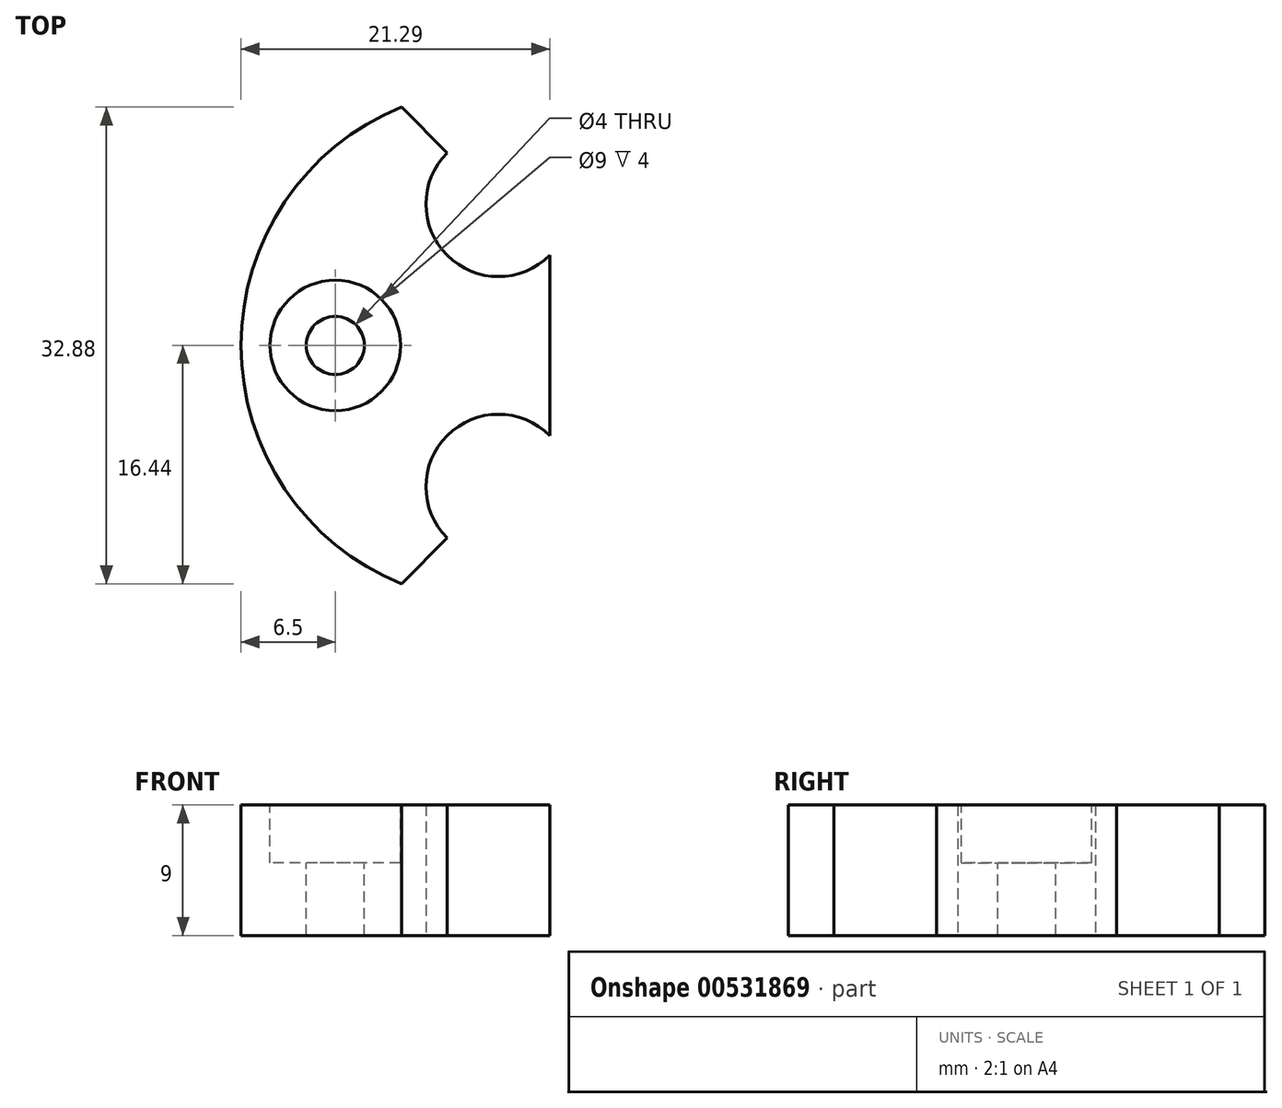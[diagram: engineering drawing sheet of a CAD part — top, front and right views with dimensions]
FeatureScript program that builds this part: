
annotation { "Feature Type Name" : "Feature", "Feature Type Description" : "" }
export const myFeature = defineFeature(function(context is Context, id is Id, definition is map)
    precondition{}
    {
        {
            var Q0;
            Q0=qCreatedBy(makeId("Top.planeOp"),FACE);
            var sketch = newSketch(context, id + "F0", { "sketchPlane" : qUnion([Q0])});
            skLineSegment(sketch, "E0", {"start": v(0, 0) * mm, "end": v(0, 50) * mm});
            skCircle(sketch, "E1", {"center": v(0, 50) * mm, "radius": 17.5 * mm});
            skLineSegment(sketch, "E2", {"start": v(0, 68.5) * mm, "end": v(0, 67.5) * mm});
            skLineSegment(sketch, "E3", {"start": v(0, 67.5) * mm, "end": v(0, 59.5) * mm});
            skLineSegment(sketch, "E4", {"start": v(0, 68.5) * mm, "end": v(0, 63.5) * mm});
            skLineSegment(sketch, "E5.1.0", {"start": v(-2.38, 63.61) * mm, "end": v(-2.38, 63.61) * mm});
            skLineSegment(sketch, "E5.2.0", {"start": v(-2.38, 55.39) * mm, "end": v(-2.38, 55.39) * mm});
            skPoint(sketch, "E5.center", {"position": v(0, 59.5) * mm});
            skLineSegment(sketch, "E6", {"start": v(-7, 59.72) * mm, "end": v(-7, 66.04) * mm});
            skLineSegment(sketch, "E7", {"start": v(7, 59.72) * mm, "end": v(7, 66.04) * mm});
            skCircle(sketch, "E8", {"center": v(0, 59.5) * mm, "radius": 4.75 * mm});
            skLineSegment(sketch, "E9", {"start": v(0, 59.5) * mm, "end": v(0, 54.5) * mm});
            skLineSegment(sketch, "E10", {"start": v(0, 54.5) * mm, "end": v(-3.14, 54.5) * mm});
            skLineSegment(sketch, "E11", {"start": v(0, 54.5) * mm, "end": v(3.14, 54.5) * mm});
            skLineSegment(sketch, "E12.trimOffspring", {"start": v(2.37, 55.39) * mm, "end": v(2.37, 55.39) * mm});
            skLineSegment(sketch, "E13", {"start": v(0, 50) * mm, "end": v(26.93, 50) * mm});
            skCircle(sketch, "E14.MirrorC", {"center": v(0, 40.5) * mm, "radius": 4.75 * mm});
            skEllipticalArc(sketch, "E15.MirrorCS", {});
            skLineSegment(sketch, "E16.MirrorCS", {"start": v(0, 45.5) * mm, "end": v(4.9, 45.5) * mm});
            skLineSegment(sketch, "E17.MirrorCS", {"start": v(0, 45.5) * mm, "end": v(-4.9, 45.5) * mm});
            skArc(sketch, "E18.MirrorCS", {"start": v(4.9, 45.5) * mm, "mid": v(6.45, 43.21) * mm, "end": v(7, 40.5) * mm});
            skArc(sketch, "E19.MirrorCS", {"start": v(-7, 40.5) * mm, "mid": v(-6.45, 43.21) * mm, "end": v(-4.9, 45.5) * mm});
            skLineSegment(sketch, "E20.MirrorCS", {"start": v(-7, 40.5) * mm, "end": v(-7, 33.96) * mm});
            skLineSegment(sketch, "E21.MirrorCS", {"start": v(7, 40.5) * mm, "end": v(7, 33.96) * mm});
            skLineSegment(sketch, "E22", {"start": v(0, 59.5) * mm, "end": v(-6.02, 66.19) * mm});
            skPoint(sketch, "E23.orphan", {"position": v(4.9, 54.5) * mm});
            skFitSpline(sketch, "E24.trimOffspring", {"points": [v(7.15, 66.46) * mm, v(6.7, 66.95) * mm, v(6.18, 67.34) * mm, v(5.4, 67.73) * mm, v(4.3, 67.95) * mm, v(2.88, 67.86) * mm, v(1.42, 67.46) * mm, v(-0.07, 66.78) * mm, v(-1.55, 65.84) * mm, v(-2.73, 64.89) * mm, v(-3.63, 64.03) * mm, v(-4.28, 63.35) * mm, v(-4.89, 62.64) * mm, v(-5.64, 61.66) * mm, v(-6.47, 60.38) * mm, v(-7.25, 58.8) * mm, v(-7.77, 57.25) * mm, v(-8.02, 55.76) * mm, v(-7.96, 54.34) * mm, v(-7.62, 53.28) * mm, v(-7.15, 52.54) * mm, v(-6.7, 52.05) * mm, v(-6.18, 51.66) * mm, v(-5.4, 51.27) * mm, v(-4.3, 51.05) * mm, v(-2.88, 51.14) * mm, v(-1.42, 51.54) * mm, v(0.07, 52.22) * mm, v(1.55, 53.16) * mm, v(2.73, 54.11) * mm, v(3.63, 54.97) * mm, v(4.28, 55.65) * mm, v(4.89, 56.36) * mm, v(5.64, 57.34) * mm, v(6.47, 58.62) * mm, v(7.25, 60.2) * mm, v(7.77, 61.75) * mm, v(8.02, 63.24) * mm, v(7.96, 64.66) * mm, v(7.62, 65.72) * mm, v(7.15, 66.46) * mm, v(6.7, 66.95) * mm, v(6.18, 67.34) * mm]});
            skFitSpline(sketch, "E25.trimOffspring", {"points": [v(-6.18, 67.34) * mm, v(-6.7, 66.95) * mm, v(-7.15, 66.46) * mm, v(-7.62, 65.72) * mm, v(-7.96, 64.66) * mm, v(-8.02, 63.24) * mm, v(-7.77, 61.75) * mm, v(-7.25, 60.2) * mm, v(-6.47, 58.62) * mm, v(-5.64, 57.34) * mm, v(-4.89, 56.36) * mm, v(-4.28, 55.65) * mm, v(-3.63, 54.97) * mm, v(-2.73, 54.11) * mm, v(-1.55, 53.16) * mm, v(-0.07, 52.22) * mm, v(1.42, 51.54) * mm, v(2.88, 51.14) * mm, v(4.3, 51.05) * mm, v(5.4, 51.27) * mm, v(6.18, 51.66) * mm, v(6.7, 52.05) * mm, v(7.15, 52.54) * mm, v(7.62, 53.28) * mm, v(7.96, 54.34) * mm, v(8.02, 55.76) * mm, v(7.77, 57.25) * mm, v(7.25, 58.8) * mm, v(6.47, 60.38) * mm, v(5.64, 61.66) * mm, v(4.89, 62.64) * mm, v(4.28, 63.35) * mm, v(3.63, 64.03) * mm, v(2.73, 64.89) * mm, v(1.55, 65.84) * mm, v(0.07, 66.78) * mm, v(-1.42, 67.46) * mm, v(-2.88, 67.86) * mm, v(-4.3, 67.95) * mm, v(-5.4, 67.73) * mm, v(-6.18, 67.34) * mm, v(-6.7, 66.95) * mm, v(-7.15, 66.46) * mm]});
            skPoint(sketch, "E26.orphan", {"position": v(-7, 59.5) * mm});
            skLineSegment(sketch, "E27", {"start": v(0, 59.5) * mm, "end": v(-3.53, 56.32) * mm});
            skLineSegment(sketch, "E28", {"start": v(0, 59.5) * mm, "end": v(6.02, 52.81) * mm});
            skEllipse(sketch, "E29", {"center": v(0, 59.5) * mm, "majorRadius": 9 * mm, "minorRadius": 4.75 * mm, "majorAxis": v(-0.67, 0.74)});
            skLineSegment(sketch, "E30", {"start": v(0, 50) * mm, "end": v(0, 68.5) * mm});
            skLineSegment(sketch, "E31", {"start": v(0, 59.5) * mm, "end": v(0, 50) * mm});
            skCircle(sketch, "E32", {"center": v(0, 59.5) * mm, "radius": 9.5 * mm});
            skCircle(sketch, "E33", {"center": v(0, 40.5) * mm, "radius": 9.5 * mm});
            skEllipse(sketch, "E34", {"center": v(0, 40.5) * mm, "majorRadius": 9.5 * mm, "minorRadius": 4.75 * mm, "majorAxis": v(0, 1)});
            skLineSegment(sketch, "E35", {"start": v(0, 50) * mm, "end": v(5.88, 50) * mm});
            skEllipse(sketch, "E36.MirrorC", {"center": v(0, 59.5) * mm, "majorRadius": 9.5 * mm, "minorRadius": 4.75 * mm, "majorAxis": v(0, -1)});
            const initialGuessF0  = {"E15.MirrorCS": [0, 0.0405, -1, 0, 0.00475, 0.009, 6.283185307179586, 3.141592653589793]};
            skSetInitialGuess(sketch, initialGuessF0);
            skSolve(sketch);
        }
        {
            var Q0;
            Q0=qCreatedBy(makeId("Top.planeOp"),FACE);
            var sketch = newSketch(context, id + "F1", { "sketchPlane" : qUnion([Q0])});
            skCircle(sketch, "E37", {"center": v(0, 0) * mm, "radius": 17.75 * mm});
            skLineSegment(sketch, "E38", {"start": v(0, 0) * mm, "end": v(0, 4.5) * mm});
            skLineSegment(sketch, "E39", {"start": v(0, 4.5) * mm, "end": v(0, 9.75) * mm});
            skCircle(sketch, "E40", {"center": v(0, 9.75) * mm, "radius": 5 * mm});
            skLineSegment(sketch, "E41", {"start": v(0, 0) * mm, "end": v(2.59, 0) * mm});
            skCircle(sketch, "E42.MirrorC", {"center": v(0, -9.75) * mm, "radius": 5 * mm});
            skSolve(sketch);
        }
        {
            var Q0;
            Q0=qSketchRegion(id+"F1",true);
            extrude(context, id + "F2", {"entities" : qUnion([Q0]), "depth" : 9 * mm});
        }
        {
            var Q0;
            Q0=makeQuery(id+"F2.opExtrude","CAP_FACE",FACE,{"disambiguationData":[OSD([sQuery(id+"F1.wireOp",EDGE,"E37"),sQuery(id+"F1.wireOp",EDGE,"E40"),sQuery(id+"F1.wireOp",EDGE,"E42.MirrorC")])],"isStart":false});
            var sketch = newSketch(context, id + "F3", { "sketchPlane" : qUnion([Q0])});
            skLineSegment(sketch, "E43", {"start": v(0, 0) * mm, "end": v(11.25, 0) * mm});
            skCircle(sketch, "E44", {"center": v(11.25, 0) * mm, "radius": 2 * mm});
            skLineSegment(sketch, "E45", {"start": v(0, 0) * mm, "end": v(0, -2.7) * mm});
            skCircle(sketch, "E46.MirrorC", {"center": v(-11.25, 0) * mm, "radius": 2 * mm});
            skSolve(sketch);
        }
        {
            var Q0;
            Q0=qSketchRegion(id+"F3",true);
            extrude(context, id + "F4", {"entities" : qUnion([Q0]), "operationType" : NewBodyOperationType.REMOVE, "oppositeDirection" : true, "depth" : 25 * mm});
        }
        {
            var Q0;
            Q0=makeQuery(id+"F2.opExtrude","CAP_FACE",FACE,{"disambiguationData":[OSD([sQuery(id+"F1.wireOp",EDGE,"E37"),sQuery(id+"F1.wireOp",EDGE,"E40"),sQuery(id+"F1.wireOp",EDGE,"E42.MirrorC")])],"isStart":false});
            var sketch = newSketch(context, id + "F5", { "sketchPlane" : qUnion([Q0])});
            skCircle(sketch, "E47", {"center": v(11.25, 0) * mm, "radius": 4.5 * mm});
            skCircle(sketch, "E48", {"center": v(-11.25, 0) * mm, "radius": 4.5 * mm});
            skSolve(sketch);
        }
        {
            var Q0;
            Q0=qSketchRegion(id+"F5",true);
            extrude(context, id + "F6", {"entities" : qUnion([Q0]), "operationType" : NewBodyOperationType.REMOVE, "oppositeDirection" : true, "depth" : 4 * mm});
        }
        {
            var Q0;
            Q0=makeQuery(id+"F2.opExtrude","CAP_FACE",FACE,{"disambiguationData":[OSD([sQuery(id+"F1.wireOp",EDGE,"E37"),sQuery(id+"F1.wireOp",EDGE,"E40"),sQuery(id+"F1.wireOp",EDGE,"E42.MirrorC")])],"isStart":false});
            var sketch = newSketch(context, id + "F7", { "sketchPlane" : qUnion([Q0])});
            skCircle(sketch, "E49", {"center": v(11.25, 0) * mm, "radius": 5 * mm});
            skSolve(sketch);
        }
        {
            var Q0;
            Q0=qSketchRegion(id+"F7",true);
            extrude(context, id + "F8", {"entities" : qUnion([Q0]), "operationType" : NewBodyOperationType.ADD, "oppositeDirection" : true, "depth" : 9 * mm});
        }
        {
            var Q0;
            Q0=makeQuery(id+"F8.boolean.opBoolean","MERGE",FACE,{"derivedFrom":[makeQuery(id+"F2.opExtrude","CAP_FACE",FACE,{"disambiguationData":[OSD([sQuery(id+"F1.wireOp",EDGE,"E37"),sQuery(id+"F1.wireOp",EDGE,"E40"),sQuery(id+"F1.wireOp",EDGE,"E42.MirrorC")])],"isStart":false}),makeQuery(id+"F8.opExtrude","CAP_FACE",FACE,{"disambiguationData":[OSD([sQuery(id+"F7.wireOp",EDGE,"E49")])],"isStart":true})]});
            var sketch = newSketch(context, id + "F9", { "sketchPlane" : qUnion([Q0])});
            skLineSegment(sketch, "E50", {"start": v(0, 0) * mm, "end": v(9.5, 0) * mm});
            skCircle(sketch, "E51", {"center": v(9.5, 0) * mm, "radius": 1.15 * mm});
            skSolve(sketch);
        }
        {
            var Q0;
            Q0=qSketchRegion(id+"F9",true);
            extrude(context, id + "F10", {"entities" : qUnion([Q0]), "operationType" : NewBodyOperationType.REMOVE, "oppositeDirection" : true, "depth" : 25 * mm});
        }
        {
            var Q0;
            Q0=makeQuery(id+"F8.boolean.opBoolean","MERGE",FACE,{"derivedFrom":[makeQuery(id+"F2.opExtrude","CAP_FACE",FACE,{"disambiguationData":[OSD([sQuery(id+"F1.wireOp",EDGE,"E37"),sQuery(id+"F1.wireOp",EDGE,"E40"),sQuery(id+"F1.wireOp",EDGE,"E42.MirrorC")])],"isStart":false}),makeQuery(id+"F8.opExtrude","CAP_FACE",FACE,{"disambiguationData":[OSD([sQuery(id+"F7.wireOp",EDGE,"E49")])],"isStart":true})]});
            var sketch = newSketch(context, id + "F11", { "sketchPlane" : qUnion([Q0])});
            skLineSegment(sketch, "E52", {"start": v(0, 9.75) * mm, "end": v(-7.43, 17.18) * mm});
            skLineSegment(sketch, "E53", {"start": v(-7.43, 17.18) * mm, "end": v(0, 9.75) * mm});
            skLineSegment(sketch, "E54", {"start": v(0, 9.75) * mm, "end": v(3.54, 6.21) * mm});
            skLineSegment(sketch, "E55", {"start": v(3.54, 6.21) * mm, "end": v(3.54, -6.21) * mm});
            skLineSegment(sketch, "E56", {"start": v(3.54, -6.21) * mm, "end": v(0, -9.75) * mm});
            skLineSegment(sketch, "E57", {"start": v(0, -9.75) * mm, "end": v(-7.43, -17.18) * mm});
            skArc(sketch, "E58", {"start": v(-7.43, -17.18) * mm, "mid": v(18.72, 0) * mm, "end": v(-7.43, 17.18) * mm});
            skSolve(sketch);
        }
        {
            var Q0;
            Q0=qSketchRegion(id+"F11",true);
            extrude(context, id + "F12", {"entities" : qUnion([Q0]), "operationType" : NewBodyOperationType.REMOVE, "oppositeDirection" : true, "depth" : 25 * mm});
        }
    });
